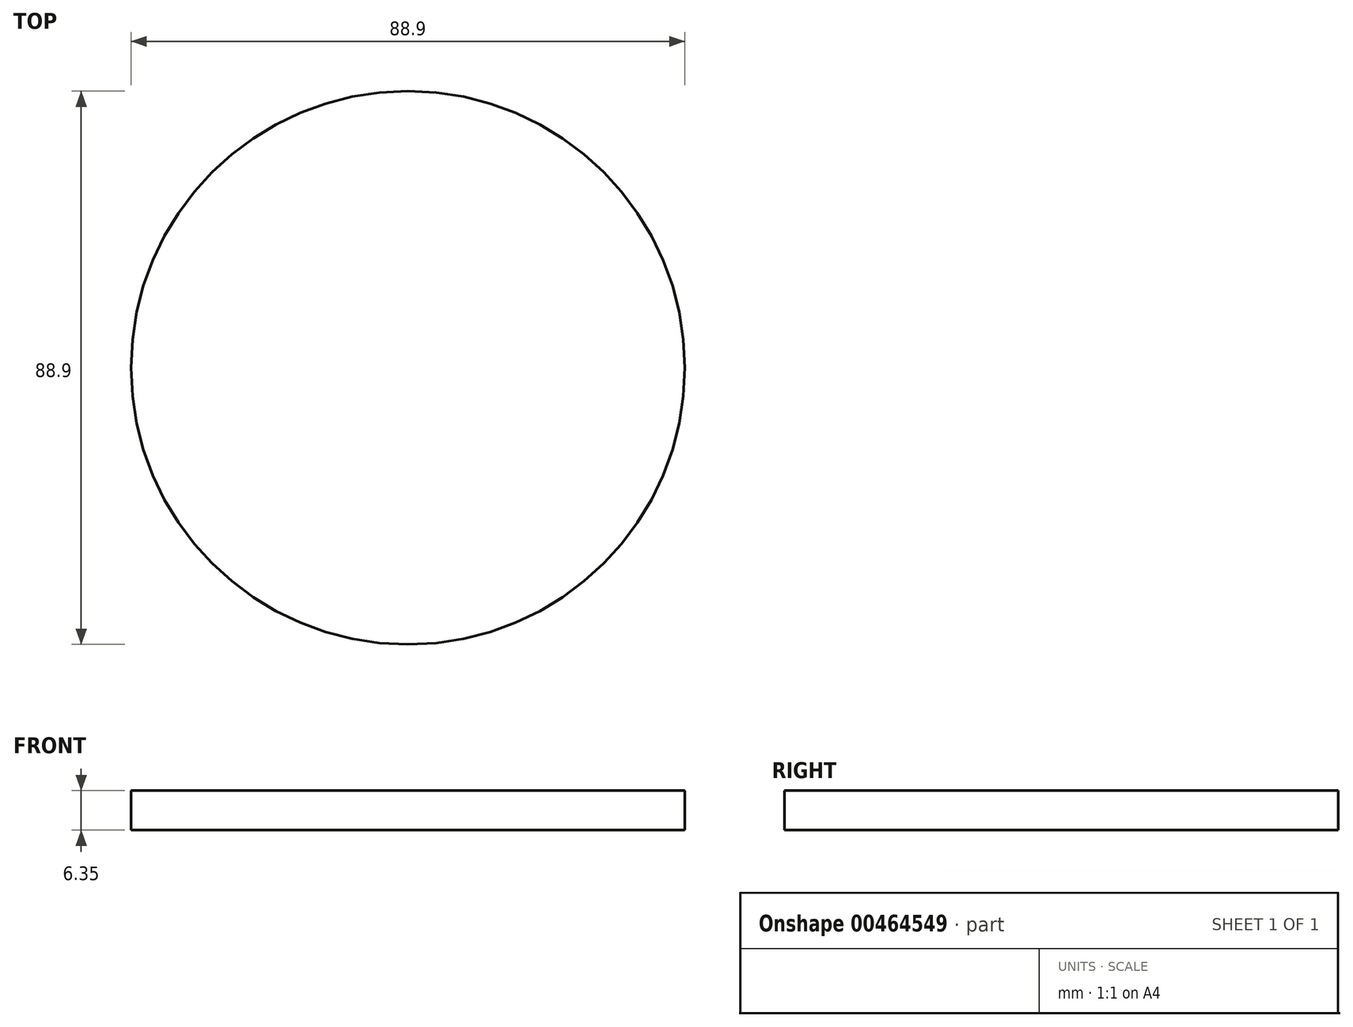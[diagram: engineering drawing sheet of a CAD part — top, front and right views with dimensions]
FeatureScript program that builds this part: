
annotation { "Feature Type Name" : "Feature", "Feature Type Description" : "" }
export const myFeature = defineFeature(function(context is Context, id is Id, definition is map)
    precondition{}
    {
        {
            var Q0;
            Q0=qCreatedBy(makeId("Top.planeOp"),FACE);
            var sketch = newSketch(context, id + "F0", { "sketchPlane" : qUnion([Q0])});
            skCircle(sketch, "E0", {"center": v(0, 0) * mm, "radius": 44.45 * mm});
            skSolve(sketch);
        }
        {
            var Q0;
            Q0=makeQuery(id+"F0.imprint","IMPRINT",FACE,{"disambiguationData":[TD([[makeQuery(id+"F0.imprint","IMPRINT",EDGE,{"derivedFrom":sQuery(id+"F0.wireOp",EDGE,"E0")}),1.0]])]});
            extrude(context, id + "F1", {"entities" : qUnion([Q0]), "depth" : 6.35 * mm});
        }
    });
